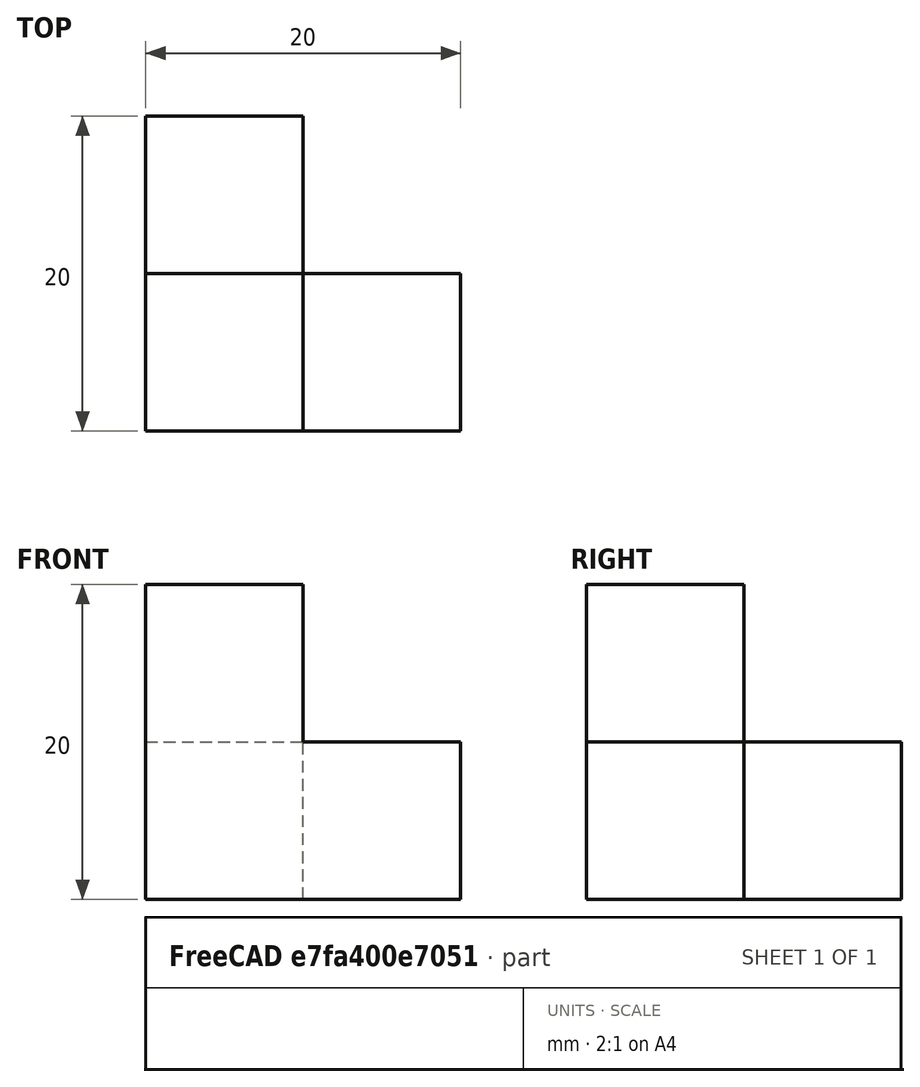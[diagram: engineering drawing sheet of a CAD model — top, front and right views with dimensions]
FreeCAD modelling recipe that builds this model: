
FCSTD DOCUMENT  (FreeCAD 0.21R33694 (Git))
Label: OJT1_T05R01_qubert
License: All rights reserved
LicenseURL: http://en.wikipedia.org/wiki/All_rights_reserved
objects: Part::Box×4, Part::MultiFuse×1
note: 5 computed .brp shape members not serialized (recipe doc carries the construction recipe); baked Part::Feature solids carry a one-line shape summary decoded from their .brp

FEATURE [Part::Box] Box  label="Cube"
  AttacherType = Attacher::AttachEngine3D
  Height = 10
  Length = 10
  Width = 10
FEATURE [Part::Box] Box001  label="Cube001"
  AttacherType = Attacher::AttachEngine3D
  Height = 10
  Length = 10
  Placement = pos=(10,0,0) rot=(0,0,1;0rad)
  Width = 10
FEATURE [Part::Box] Box002  label="Cube002"
  AttacherType = Attacher::AttachEngine3D
  Height = 10
  Length = 10
  Placement = pos=(0,10,0) rot=(0,0,1;0rad)
  Width = 10
FEATURE [Part::Box] Box003  label="Cube003"
  AttacherType = Attacher::AttachEngine3D
  Height = 10
  Length = 10
  Placement = pos=(0,0,10) rot=(0,0,1;0rad)
  Width = 10
FEATURE [Part::MultiFuse] Fusion
  Refine = true
  Shapes = -> [Box003,Box002,Box001,Box]
